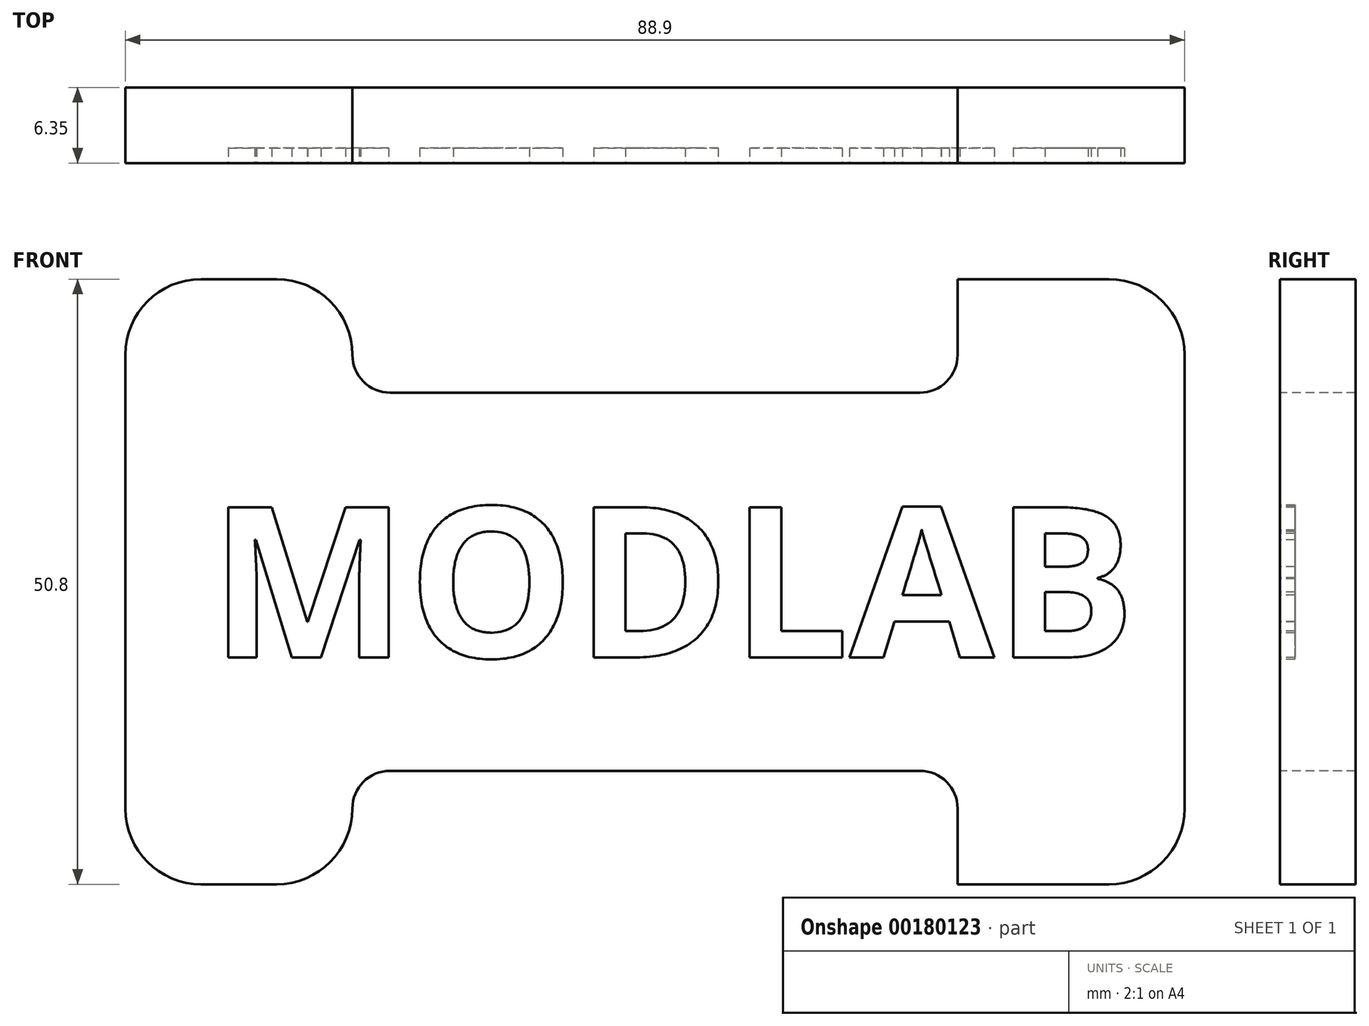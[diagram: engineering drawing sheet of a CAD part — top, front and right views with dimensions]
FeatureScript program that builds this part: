
annotation { "Feature Type Name" : "Feature", "Feature Type Description" : "" }
export const myFeature = defineFeature(function(context is Context, id is Id, definition is map)
    precondition{}
    {
        {
            var Q0;
            Q0=qCreatedBy(makeId("Front.planeOp"),FACE);
            var sketch = newSketch(context, id + "F0", { "sketchPlane" : qUnion([Q0])});
            skLineSegment(sketch, "E0.bottom", {"start": v(44.45, 25.4) * mm, "end": v(-44.45, 25.4) * mm});
            skLineSegment(sketch, "E0.top", {"start": v(44.45, -25.4) * mm, "end": v(-44.45, -25.4) * mm});
            skLineSegment(sketch, "E0.left", {"start": v(44.45, 25.4) * mm, "end": v(44.45, -25.4) * mm});
            skLineSegment(sketch, "E0.right", {"start": v(-44.45, 25.4) * mm, "end": v(-44.45, -25.4) * mm});
            skPoint(sketch, "E0.middle", {"position": v(0, 0) * mm});
            skSolve(sketch);
        }
        {
            var Q0;
            Q0=makeQuery(id+"F0.imprint","IMPRINT",FACE,{"disambiguationData":[TD([[makeQuery(id+"F0.imprint","IMPRINT",EDGE,{"derivedFrom":sQuery(id+"F0.wireOp",EDGE,"E0.bottom")}),1.0]])]});
            extrude(context, id + "F1", {"entities" : qUnion([Q0]), "depth" : 6.35 * mm});
        }
        {
            var Q0;
            Q0=makeQuery(id+"F1.opExtrude","CAP_FACE",FACE,{"disambiguationData":[OSD([sQuery(id+"F0.wireOp",EDGE,"E0.bottom"),sQuery(id+"F0.wireOp",EDGE,"E0.top"),sQuery(id+"F0.wireOp",EDGE,"E0.left"),sQuery(id+"F0.wireOp",EDGE,"E0.right")])],"isStart":false});
            var sketch = newSketch(context, id + "F2", { "sketchPlane" : qUnion([Q0])});
            skLineSegment(sketch, "E1.bottom", {"start": v(-25.4, 25.4) * mm, "end": v(25.4, 25.4) * mm});
            skLineSegment(sketch, "E1.top", {"start": v(-25.4, 15.88) * mm, "end": v(25.4, 15.88) * mm});
            skLineSegment(sketch, "E1.left", {"start": v(-25.4, 25.4) * mm, "end": v(-25.4, 15.88) * mm});
            skLineSegment(sketch, "E1.right", {"start": v(25.4, 25.4) * mm, "end": v(25.4, 15.88) * mm});
            skLineSegment(sketch, "E2", {"start": v(0, 0) * mm, "end": v(0, 25.4) * mm, "construction": true});
            skLineSegment(sketch, "E3", {"start": v(-44.45, 0) * mm, "end": v(44.45, 0) * mm, "construction": true});
            skLineSegment(sketch, "E4.MirrorCS", {"start": v(-25.4, -15.88) * mm, "end": v(25.4, -15.88) * mm});
            skLineSegment(sketch, "E5.MirrorCS", {"start": v(-25.4, -25.4) * mm, "end": v(-25.4, -15.88) * mm});
            skLineSegment(sketch, "E6.MirrorCS", {"start": v(-25.4, -25.4) * mm, "end": v(25.4, -25.4) * mm});
            skLineSegment(sketch, "E7.MirrorCS", {"start": v(25.4, -25.4) * mm, "end": v(25.4, -15.87) * mm});
            skSolve(sketch);
        }
        {
            var Q0;
            Q0=makeQuery(id+"F2.imprint","IMPRINT",FACE,{"disambiguationData":[TD([[makeQuery(id+"F2.imprint","IMPRINT",EDGE,{"derivedFrom":sQuery(id+"F2.wireOp",EDGE,"E1.bottom")}),1.0]])]});
            var Q1;
            Q1=makeQuery(id+"F2.imprint","IMPRINT",FACE,{"disambiguationData":[TD([[makeQuery(id+"F2.imprint","IMPRINT",EDGE,{"derivedFrom":sQuery(id+"F2.wireOp",EDGE,"E4.MirrorCS")}),-1.0]])]});
            extrude(context, id + "F3", {"entities" : qUnion([Q0, Q1]), "operationType" : NewBodyOperationType.REMOVE, "oppositeDirection" : true, "depth" : 6.35 * mm});
        }
        {
            var Q0;
            Q0=makeQuery(id+"F1.opExtrude","SWEPT_EDGE",EDGE,{"disambiguationData":[OSD([sQuery(id+"F0.wireOp",EDGE,"E0.bottom"),sQuery(id+"F0.wireOp",EDGE,"E0.right")])]});
            var Q1;
            Q1=makeQuery(id+"F1.opExtrude","SWEPT_EDGE",EDGE,{"disambiguationData":[OSD([sQuery(id+"F0.wireOp",EDGE,"E0.top"),sQuery(id+"F0.wireOp",EDGE,"E0.right")])]});
            var Q2;
            Q2=makeQuery(id+"F1.opExtrude","SWEPT_EDGE",EDGE,{"disambiguationData":[OSD([sQuery(id+"F0.wireOp",EDGE,"E0.top"),sQuery(id+"F0.wireOp",EDGE,"E0.left")])]});
            var Q3;
            Q3=makeQuery(id+"F1.opExtrude","SWEPT_EDGE",EDGE,{"disambiguationData":[OSD([sQuery(id+"F0.wireOp",EDGE,"E0.bottom"),sQuery(id+"F0.wireOp",EDGE,"E0.left")])]});
            var Q4;
            Q4=makeQuery(id+"F3.boolean.opBoolean","COPY",EDGE,{"derivedFrom":makeQuery(id+"F3.opExtrude","SWEPT_EDGE",EDGE,{"disambiguationData":[OSD([sQuery(id+"F0.wireOp",EDGE,"E0.bottom"),sQuery(id+"F2.wireOp",EDGE,"E1.bottom"),sQuery(id+"F2.wireOp",EDGE,"E1.left")])]})});
            var Q5;
            Q5=makeQuery(id+"F3.boolean.opBoolean","COPY",EDGE,{"derivedFrom":makeQuery(id+"F3.opExtrude","SWEPT_EDGE",EDGE,{"disambiguationData":[OSD([sQuery(id+"F0.wireOp",EDGE,"E0.top"),sQuery(id+"F2.wireOp",EDGE,"E5.MirrorCS"),sQuery(id+"F2.wireOp",EDGE,"E6.MirrorCS")])]})});
            var Q6;
            Q6=makeQuery(id+"F3.boolean.opBoolean","COPY",EDGE,{"derivedFrom":makeQuery(id+"F3.opExtrude","SWEPT_EDGE",EDGE,{"disambiguationData":[OSD([sQuery(id+"F0.wireOp",EDGE,"E0.bottom"),sQuery(id+"F2.wireOp",EDGE,"E1.bottom"),sQuery(id+"F2.wireOp",EDGE,"E1.right")])]})});
            var Q7;
            Q7=makeQuery(id+"F3.boolean.opBoolean","COPY",EDGE,{"derivedFrom":makeQuery(id+"F3.opExtrude","SWEPT_EDGE",EDGE,{"disambiguationData":[OSD([sQuery(id+"F0.wireOp",EDGE,"E0.top"),sQuery(id+"F2.wireOp",EDGE,"E6.MirrorCS"),sQuery(id+"F2.wireOp",EDGE,"E7.MirrorCS")])]})});
            fillet(context, id + "F4", {"entities" : qUnion([Q0, Q1, Q2, Q3, Q4, Q5, Q6, Q7]), "radius" : 6.35 * mm, "tangentPropagation" : true, "allowEdgeOverflow" : false});
        }
        {
            var Q0;
            Q0=makeQuery(id+"F3.boolean.opBoolean","COPY",EDGE,{"derivedFrom":makeQuery(id+"F3.opExtrude","SWEPT_EDGE",EDGE,{"disambiguationData":[OSD([sQuery(id+"F2.wireOp",EDGE,"E1.top"),sQuery(id+"F2.wireOp",EDGE,"E1.left")])]})});
            var Q1;
            Q1=makeQuery(id+"F3.boolean.opBoolean","COPY",EDGE,{"derivedFrom":makeQuery(id+"F3.opExtrude","SWEPT_EDGE",EDGE,{"disambiguationData":[OSD([sQuery(id+"F2.wireOp",EDGE,"E1.top"),sQuery(id+"F2.wireOp",EDGE,"E1.right")])]})});
            var Q2;
            Q2=makeQuery(id+"F3.boolean.opBoolean","COPY",EDGE,{"derivedFrom":makeQuery(id+"F3.opExtrude","SWEPT_EDGE",EDGE,{"disambiguationData":[OSD([sQuery(id+"F2.wireOp",EDGE,"E4.MirrorCS"),sQuery(id+"F2.wireOp",EDGE,"E5.MirrorCS")])]})});
            var Q3;
            Q3=makeQuery(id+"F3.boolean.opBoolean","COPY",EDGE,{"derivedFrom":makeQuery(id+"F3.opExtrude","SWEPT_EDGE",EDGE,{"disambiguationData":[OSD([sQuery(id+"F2.wireOp",EDGE,"E4.MirrorCS"),sQuery(id+"F2.wireOp",EDGE,"E7.MirrorCS")])]})});
            fillet(context, id + "F5", {"entities" : qUnion([Q0, Q1, Q2, Q3]), "radius" : 3.17 * mm, "tangentPropagation" : true, "allowEdgeOverflow" : false});
        }
        {
            var Q0;
            Q0=makeQuery(id+"F1.opExtrude","CAP_FACE",FACE,{"disambiguationData":[OSD([sQuery(id+"F0.wireOp",EDGE,"E0.bottom"),sQuery(id+"F0.wireOp",EDGE,"E0.top"),sQuery(id+"F0.wireOp",EDGE,"E0.left"),sQuery(id+"F0.wireOp",EDGE,"E0.right")])],"isStart":false});
            var sketch = newSketch(context, id + "F6", { "sketchPlane" : qUnion([Q0])});
            skText(sketch, "E8", { "text": "MODLAB", "fontName": "OpenSans-Bold.ttf"});
            const initialGuessF6  = {"E8": [-0.03739, -0.00635, 1, 0, 0.0127]};
            skSetInitialGuess(sketch, initialGuessF6);
            skSolve(sketch);
        }
        {
            var Q0;
            Q0 = qSketchRegion(id + "F6", true);
            extrude(context, id + "F7", {"entities" : qUnion([Q0]), "operationType" : NewBodyOperationType.REMOVE, "oppositeDirection" : true, "depth" : 1.27 * mm});
        }
    });
